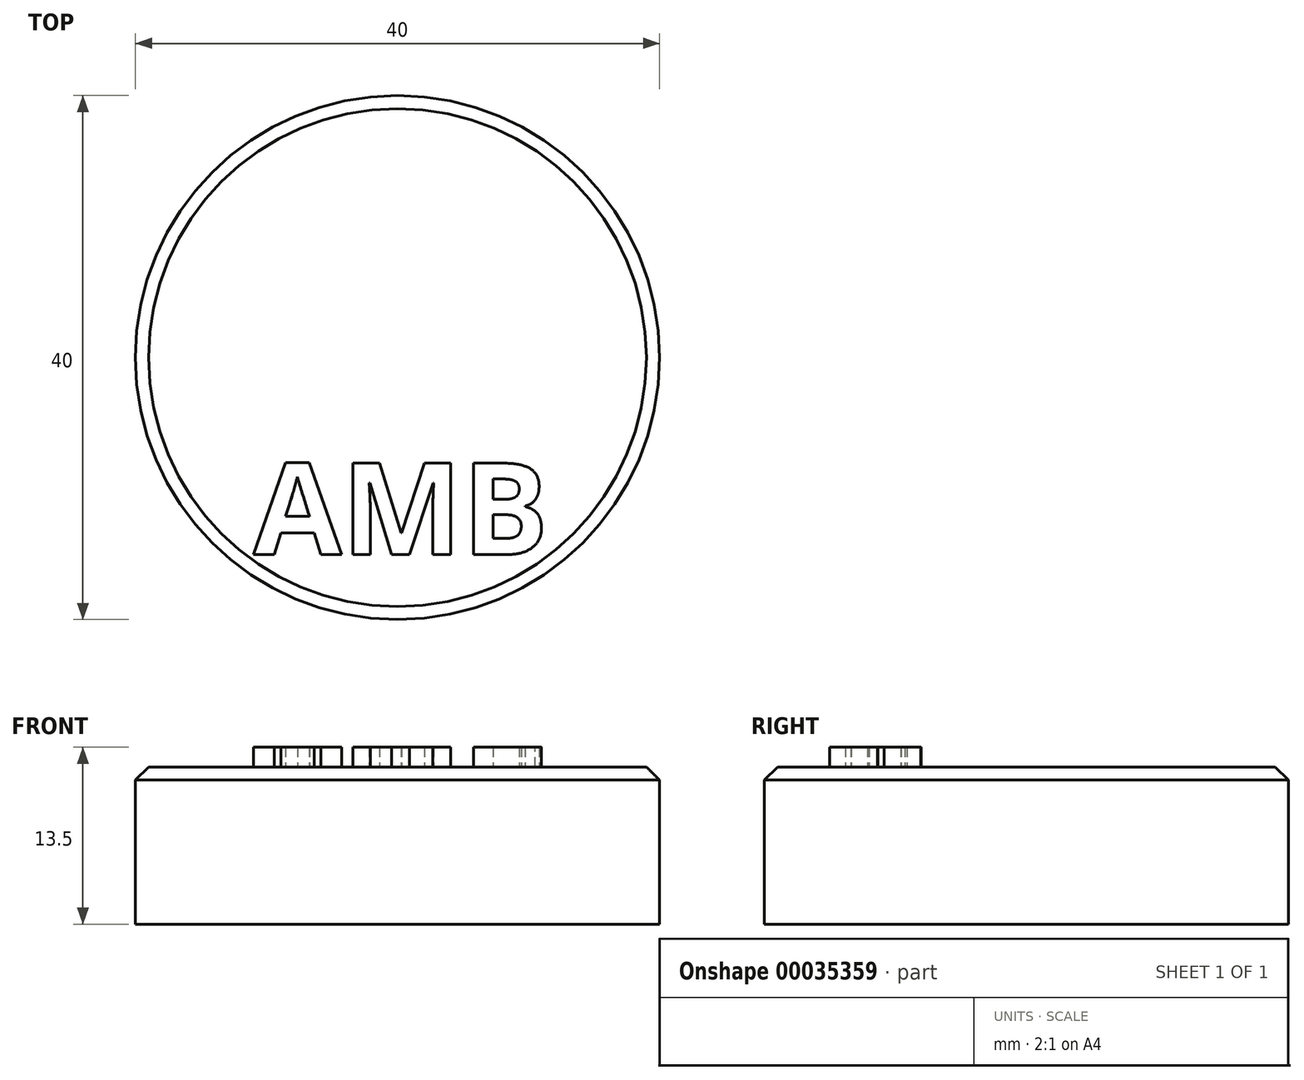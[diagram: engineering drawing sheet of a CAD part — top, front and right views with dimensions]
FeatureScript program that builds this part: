
annotation { "Feature Type Name" : "Feature", "Feature Type Description" : "" }
export const myFeature = defineFeature(function(context is Context, id is Id, definition is map)
    precondition{}
    {
        {
            var Q0;
            Q0=qCreatedBy(makeId("Top.planeOp"),FACE);
            var sketch = newSketch(context, id + "F0", { "sketchPlane" : qUnion([Q0])});
            skCircle(sketch, "E0", {"center": v(0, 0) * mm, "radius": 20 * mm});
            skSolve(sketch);
        }
        {
            var Q0;
            Q0=makeQuery(id+"F0.imprint","IMPRINT",FACE,{"disambiguationData":[TD([[makeQuery(id+"F0.imprint","IMPRINT",EDGE,{"derivedFrom":sQuery(id+"F0.wireOp",EDGE,"E0")}),1.0]])]});
            extrude(context, id + "F1", {"entities" : qUnion([Q0]), "depth" : 12 * mm});
        }
        {
            var Q0;
            Q0=makeQuery(id+"F1.opExtrude","CAP_FACE",FACE,{"disambiguationData":[OSD([sQuery(id+"F0.wireOp",EDGE,"E0"),sQuery(id+"F0.wireOp",EDGE,"e01d2289-4002-4c23-aa61-1d29497965a0")])],"isStart":false});
            var sketch = newSketch(context, id + "F2", { "sketchPlane" : qUnion([Q0])});
            skText(sketch, "E1", { "text": "AMB", "fontName": "OpenSans-Bold.ttf"});
            const initialGuessF2  = {"E1": [-0.011, -0.01503, 1, 0, 0.00703]};
            skSetInitialGuess(sketch, initialGuessF2);
            skSolve(sketch);
        }
        {
            var Q0;
            Q0 = qSketchRegion(id + "F2", true);
            extrude(context, id + "F3", {"entities" : qUnion([Q0]), "operationType" : NewBodyOperationType.ADD, "depth" : 1.5 * mm});
        }
        {
            var Q0;
            Q0=makeQuery(id+"F1.opExtrude","CAP_EDGE",EDGE,{"disambiguationData":[OSD([sQuery(id+"F0.wireOp",EDGE,"E0")])],"isStart":false});
            chamfer(context, id + "F4", {"entities" : qUnion([Q0]), "width" : 1 * mm, "tangentPropagation" : true});
        }
    });
